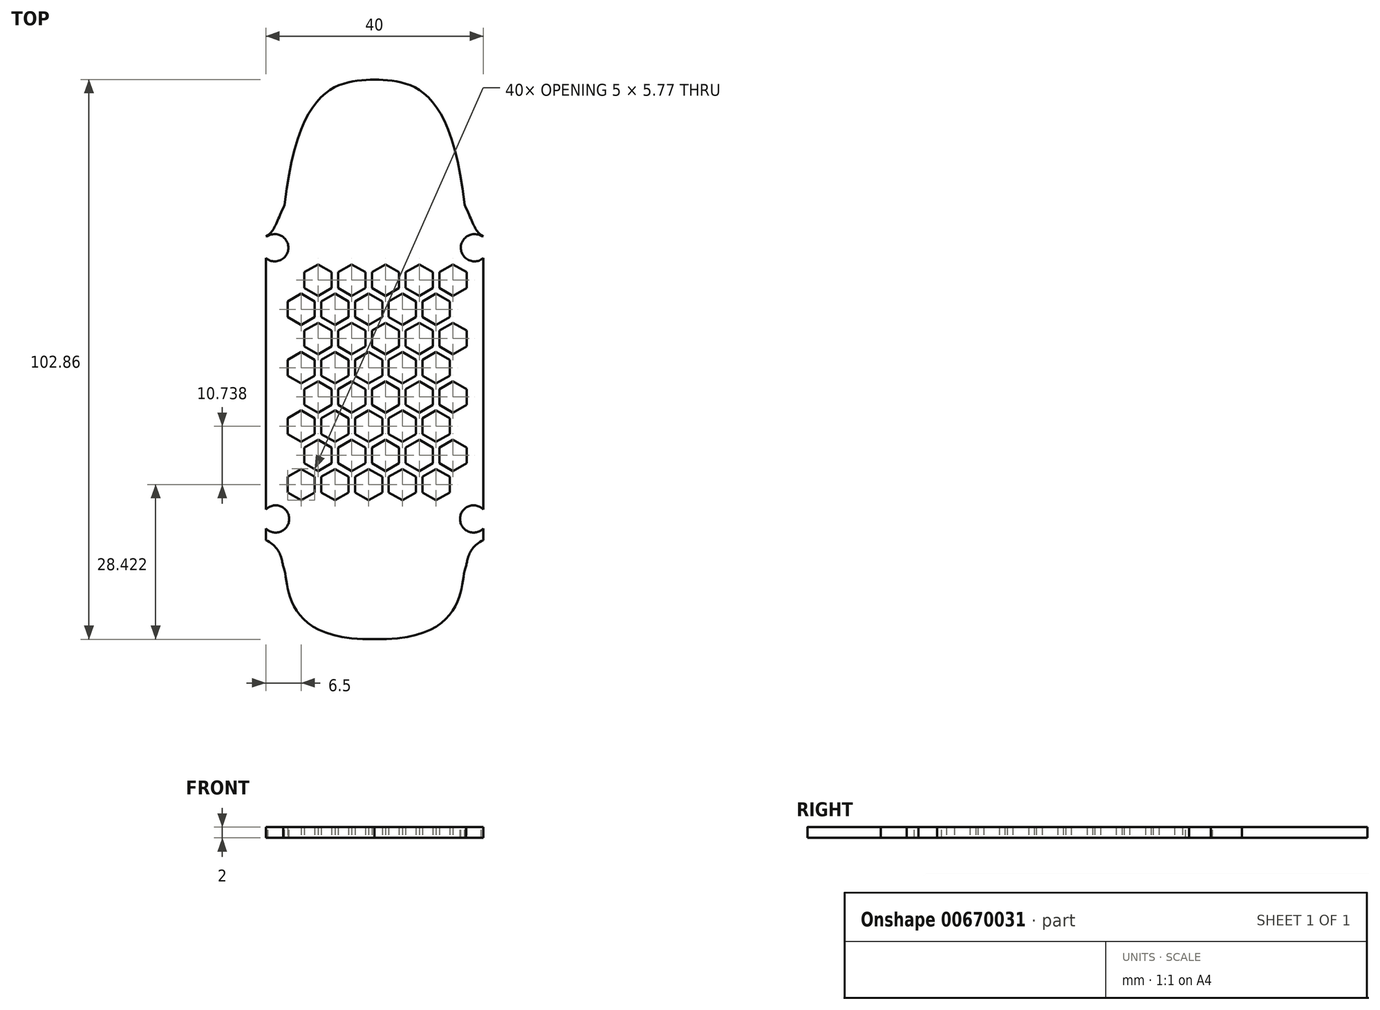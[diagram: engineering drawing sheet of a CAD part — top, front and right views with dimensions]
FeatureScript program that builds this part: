
annotation { "Feature Type Name" : "Feature", "Feature Type Description" : "" }
export const myFeature = defineFeature(function(context is Context, id is Id, definition is map)
    precondition{}
    {
        {
            var Q0;
            Q0=qCreatedBy(makeId("Top.planeOp"),FACE);
            var sketch = newSketch(context, id + "F0", { "sketchPlane" : qUnion([Q0])});
            skLineSegment(sketch, "E0", {"start": v(20, 27.95) * mm, "end": v(20, -27.95) * mm});
            skLineSegment(sketch, "E1", {"start": v(20, -27.95) * mm, "end": v(-20, -27.95) * mm});
            skLineSegment(sketch, "E2", {"start": v(-20, -27.95) * mm, "end": v(-20, 27.95) * mm});
            skLineSegment(sketch, "E3", {"start": v(-20, 27.95) * mm, "end": v(20, 27.95) * mm});
            skPoint(sketch, "E4", {"position": v(0, 0) * mm});
            skPoint(sketch, "E4.positionSnap0", {"position": v(0, 27.95) * mm});
            skPoint(sketch, "E5", {"position": v(-20, 0) * mm});
            skFitSpline(sketch, "E6", {"points": [v(0, 56.71) * mm, v(-16.53, 33.68) * mm], "startDerivative": vector(-17.27, -1.25) * mm, "endDerivative": vector(-7.65, -70.35) * mm});
            skFitSpline(sketch, "E7", {"points": [v(-16.53, 33.68) * mm, v(-20, 27.95) * mm], "startDerivative": vector(-5.62, -11.68) * mm, "endDerivative": vector(-4.8, -2.18) * mm});
            skLineSegment(sketch, "E8", {"start": v(0, 60.75) * mm, "end": v(0, -48.18) * mm, "construction": true});
            skFitSpline(sketch, "E9.MirrorCS", {"points": [v(0, 56.71) * mm, v(16.53, 33.68) * mm], "startDerivative": vector(17.27, -1.25) * mm, "endDerivative": vector(7.65, -70.35) * mm});
            skFitSpline(sketch, "E10.MirrorCS", {"points": [v(16.53, 33.68) * mm, v(20, 27.95) * mm], "startDerivative": vector(5.62, -11.68) * mm, "endDerivative": vector(4.8, -2.18) * mm});
            skFitSpline(sketch, "E11", {"points": [v(20, -27.95) * mm, v(16.8, -32.7) * mm], "startDerivative": vector(-8.06, -3.46) * mm, "endDerivative": vector(-0.94, -3.81) * mm});
            skFitSpline(sketch, "E12", {"points": [v(16.8, -32.7) * mm, v(0, -46.14) * mm], "startDerivative": vector(-3.62, -7.41) * mm, "endDerivative": vector(-53.21, 1.16) * mm});
            skFitSpline(sketch, "E13.MirrorCS", {"points": [v(-16.8, -32.7) * mm, v(0, -46.14) * mm], "startDerivative": vector(3.62, -7.41) * mm, "endDerivative": vector(53.21, 1.16) * mm});
            skFitSpline(sketch, "E14.MirrorCS", {"points": [v(-20, -27.95) * mm, v(-16.8, -32.7) * mm], "startDerivative": vector(8.06, -3.46) * mm, "endDerivative": vector(0.94, -3.81) * mm});
            skCircle(sketch, "E15", {"center": v(18.34, 25.8) * mm, "radius": 2.5 * mm});
            skCircle(sketch, "E16.MirrorC", {"center": v(-18.34, 25.8) * mm, "radius": 2.5 * mm});
            skCircle(sketch, "E17", {"center": v(18.2, -24.04) * mm, "radius": 2.5 * mm});
            skCircle(sketch, "E18.MirrorC", {"center": v(-18.2, -24.04) * mm, "radius": 2.5 * mm});
            skSolve(sketch);
        }
        {
            var Q0;
            Q0=makeQuery(id+"F0.imprint","IMPRINT",FACE,{"disambiguationData":[TD([[makeQuery(id+"F0.imprint","IMPRINT",EDGE,{"derivedFrom":sQuery(id+"F0.wireOp",EDGE,"E1")}),1.0]])]});
            var Q1;
            Q1=makeQuery(id+"F0.imprint","IMPRINT",FACE,{"disambiguationData":[TD([[makeQuery(id+"F0.imprint","IMPRINT",EDGE,{"derivedFrom":sQuery(id+"F0.wireOp",EDGE,"E3")}),1.0]])]});
            var Q2;
            {var subQ1=sQuery(id+"F0.wireOp",EDGE,"E1");Q2=makeQuery(id+"F0.imprint","IMPRINT",FACE,{"disambiguationData":[TD([[makeQuery(id+"F0.imprint","IMPRINT",EDGE,{"derivedFrom":subQ1}),-1.0]])]});}
            extrude(context, id + "F1", {"entities" : qUnion([Q0, Q1, Q2]), "oppositeDirection" : true, "depth" : 2 * mm, "offsetDistance" : 25 * mm});
        }
        {
            var Q0;
            Q0=makeQuery(id+"F1.opExtrude","CAP_FACE",FACE,{"disambiguationData":[OSD([sQuery(id+"F0.wireOp",EDGE,"E0"),sQuery(id+"F0.wireOp",EDGE,"E2"),sQuery(id+"F0.wireOp",EDGE,"E3"),sQuery(id+"F0.wireOp",EDGE,"E6"),sQuery(id+"F0.wireOp",EDGE,"E7"),sQuery(id+"F0.wireOp",EDGE,"E9.MirrorCS"),sQuery(id+"F0.wireOp",EDGE,"E10.MirrorCS"),sQuery(id+"F0.wireOp",EDGE,"E11"),sQuery(id+"F0.wireOp",EDGE,"E12"),sQuery(id+"F0.wireOp",EDGE,"E13.MirrorCS"),sQuery(id+"F0.wireOp",EDGE,"E14.MirrorCS"),sQuery(id+"F0.wireOp",EDGE,"E15"),sQuery(id+"F0.wireOp",EDGE,"E16.MirrorC"),sQuery(id+"F0.wireOp",EDGE,"E17"),sQuery(id+"F0.wireOp",EDGE,"E18.MirrorC")])],"isStart":false});
            var sketch = newSketch(context, id + "F2", { "sketchPlane" : qUnion([Q0])});
            skCircle(sketch, "E19.cCircle", {"center": v(-13.5, 17.73) * mm, "radius": 2.5 * mm, "construction": true});
            skLineSegment(sketch, "E19.0", {"start": v(-11, 19.17) * mm, "end": v(-11, 16.28) * mm});
            skLineSegment(sketch, "E19.1", {"start": v(-11, 16.28) * mm, "end": v(-13.5, 14.84) * mm});
            skLineSegment(sketch, "E19.2", {"start": v(-13.5, 14.84) * mm, "end": v(-16, 16.28) * mm});
            skLineSegment(sketch, "E19.3", {"start": v(-16, 16.28) * mm, "end": v(-16, 19.17) * mm});
            skLineSegment(sketch, "E19.4", {"start": v(-16, 19.17) * mm, "end": v(-13.5, 20.62) * mm});
            skLineSegment(sketch, "E19.5", {"start": v(-13.5, 20.62) * mm, "end": v(-11, 19.17) * mm});
            skPoint(sketch, "E19.0.midPoint", {"position": v(-11, 17.73) * mm});
            skCircle(sketch, "E20.cCircle", {"center": v(-10.4, 12.36) * mm, "radius": 2.5 * mm, "construction": true});
            skLineSegment(sketch, "E20.0", {"start": v(-7.9, 13.8) * mm, "end": v(-7.9, 10.92) * mm});
            skLineSegment(sketch, "E20.1", {"start": v(-7.9, 10.92) * mm, "end": v(-10.4, 9.47) * mm});
            skLineSegment(sketch, "E20.2", {"start": v(-10.4, 9.47) * mm, "end": v(-12.9, 10.92) * mm});
            skLineSegment(sketch, "E20.3", {"start": v(-12.9, 10.92) * mm, "end": v(-12.9, 13.8) * mm});
            skLineSegment(sketch, "E20.4", {"start": v(-12.9, 13.8) * mm, "end": v(-10.4, 15.25) * mm});
            skLineSegment(sketch, "E20.5", {"start": v(-10.4, 15.25) * mm, "end": v(-7.9, 13.8) * mm});
            skPoint(sketch, "E20.0.midPoint", {"position": v(-7.9, 12.36) * mm});
            skCircle(sketch, "E21.0.1.0", {"center": v(-10.4, 1.62) * mm, "radius": 2.5 * mm, "construction": true});
            skCircle(sketch, "E21.0.1.1", {"center": v(-13.5, 7) * mm, "radius": 2.5 * mm, "construction": true});
            skLineSegment(sketch, "E21.0.1.2", {"start": v(-11, 8.43) * mm, "end": v(-11, 5.55) * mm});
            skLineSegment(sketch, "E21.0.1.3", {"start": v(-11, 5.55) * mm, "end": v(-13.5, 4.1) * mm});
            skLineSegment(sketch, "E21.0.1.4", {"start": v(-13.5, 4.1) * mm, "end": v(-16, 5.55) * mm});
            skLineSegment(sketch, "E21.0.1.5", {"start": v(-16, 5.55) * mm, "end": v(-16, 8.43) * mm});
            skLineSegment(sketch, "E21.0.1.6", {"start": v(-16, 8.43) * mm, "end": v(-13.5, 9.88) * mm});
            skLineSegment(sketch, "E21.0.1.7", {"start": v(-13.5, 9.88) * mm, "end": v(-11, 8.43) * mm});
            skLineSegment(sketch, "E21.0.1.8", {"start": v(-7.9, 0.18) * mm, "end": v(-10.4, -1.27) * mm});
            skLineSegment(sketch, "E21.0.1.9", {"start": v(-10.4, -1.27) * mm, "end": v(-12.9, 0.18) * mm});
            skLineSegment(sketch, "E21.0.1.10", {"start": v(-12.9, 3.06) * mm, "end": v(-10.4, 4.5) * mm});
            skPoint(sketch, "E21.0.1.11", {"position": v(-7.9, 1.62) * mm});
            skPoint(sketch, "E21.0.1.12", {"position": v(-11, 7) * mm});
            skLineSegment(sketch, "E21.0.1.13", {"start": v(-10.4, 4.5) * mm, "end": v(-7.9, 3.06) * mm});
            skLineSegment(sketch, "E21.0.1.14", {"start": v(-7.9, 3.06) * mm, "end": v(-7.9, 0.18) * mm});
            skLineSegment(sketch, "E21.0.1.15", {"start": v(-12.9, 0.18) * mm, "end": v(-12.9, 3.06) * mm});
            skCircle(sketch, "E21.0.2.0", {"center": v(-10.4, -9.12) * mm, "radius": 2.5 * mm, "construction": true});
            skCircle(sketch, "E21.0.2.1", {"center": v(-13.5, -3.75) * mm, "radius": 2.5 * mm, "construction": true});
            skLineSegment(sketch, "E21.0.2.2", {"start": v(-11, -2.3) * mm, "end": v(-11, -5.2) * mm});
            skLineSegment(sketch, "E21.0.2.3", {"start": v(-11, -5.2) * mm, "end": v(-13.5, -6.63) * mm});
            skLineSegment(sketch, "E21.0.2.4", {"start": v(-13.5, -6.63) * mm, "end": v(-16, -5.2) * mm});
            skLineSegment(sketch, "E21.0.2.5", {"start": v(-16, -5.2) * mm, "end": v(-16, -2.3) * mm});
            skLineSegment(sketch, "E21.0.2.6", {"start": v(-16, -2.3) * mm, "end": v(-13.5, -0.86) * mm});
            skLineSegment(sketch, "E21.0.2.7", {"start": v(-13.5, -0.86) * mm, "end": v(-11, -2.3) * mm});
            skLineSegment(sketch, "E21.0.2.8", {"start": v(-7.9, -10.56) * mm, "end": v(-10.4, -12) * mm});
            skLineSegment(sketch, "E21.0.2.9", {"start": v(-10.4, -12) * mm, "end": v(-12.9, -10.56) * mm});
            skLineSegment(sketch, "E21.0.2.10", {"start": v(-12.9, -7.67) * mm, "end": v(-10.4, -6.23) * mm});
            skPoint(sketch, "E21.0.2.11", {"position": v(-7.9, -9.12) * mm});
            skPoint(sketch, "E21.0.2.12", {"position": v(-11, -3.75) * mm});
            skLineSegment(sketch, "E21.0.2.13", {"start": v(-10.4, -6.23) * mm, "end": v(-7.9, -7.67) * mm});
            skLineSegment(sketch, "E21.0.2.14", {"start": v(-7.9, -7.67) * mm, "end": v(-7.9, -10.56) * mm});
            skLineSegment(sketch, "E21.0.2.15", {"start": v(-12.9, -10.56) * mm, "end": v(-12.9, -7.67) * mm});
            skCircle(sketch, "E21.0.3.0", {"center": v(-10.4, -19.86) * mm, "radius": 2.5 * mm, "construction": true});
            skCircle(sketch, "E21.0.3.1", {"center": v(-13.5, -14.49) * mm, "radius": 2.5 * mm, "construction": true});
            skLineSegment(sketch, "E21.0.3.2", {"start": v(-11, -13.04) * mm, "end": v(-11, -15.93) * mm});
            skLineSegment(sketch, "E21.0.3.3", {"start": v(-11, -15.93) * mm, "end": v(-13.5, -17.37) * mm});
            skLineSegment(sketch, "E21.0.3.4", {"start": v(-13.5, -17.37) * mm, "end": v(-16, -15.93) * mm});
            skLineSegment(sketch, "E21.0.3.5", {"start": v(-16, -15.93) * mm, "end": v(-16, -13.04) * mm});
            skLineSegment(sketch, "E21.0.3.6", {"start": v(-16, -13.04) * mm, "end": v(-13.5, -11.6) * mm});
            skLineSegment(sketch, "E21.0.3.7", {"start": v(-13.5, -11.6) * mm, "end": v(-11, -13.04) * mm});
            skLineSegment(sketch, "E21.0.3.8", {"start": v(-7.9, -21.3) * mm, "end": v(-10.4, -22.74) * mm});
            skLineSegment(sketch, "E21.0.3.9", {"start": v(-10.4, -22.74) * mm, "end": v(-12.9, -21.3) * mm});
            skLineSegment(sketch, "E21.0.3.10", {"start": v(-12.9, -18.41) * mm, "end": v(-10.4, -16.97) * mm});
            skPoint(sketch, "E21.0.3.11", {"position": v(-7.9, -19.86) * mm});
            skPoint(sketch, "E21.0.3.12", {"position": v(-11, -14.49) * mm});
            skLineSegment(sketch, "E21.0.3.13", {"start": v(-10.4, -16.97) * mm, "end": v(-7.9, -18.41) * mm});
            skLineSegment(sketch, "E21.0.3.14", {"start": v(-7.9, -18.41) * mm, "end": v(-7.9, -21.3) * mm});
            skLineSegment(sketch, "E21.0.3.15", {"start": v(-12.9, -21.3) * mm, "end": v(-12.9, -18.41) * mm});
            skCircle(sketch, "E21.1.0.0", {"center": v(-4.2, 12.36) * mm, "radius": 2.5 * mm, "construction": true});
            skCircle(sketch, "E21.1.0.1", {"center": v(-7.3, 17.73) * mm, "radius": 2.5 * mm, "construction": true});
            skLineSegment(sketch, "E21.1.0.2", {"start": v(-4.8, 19.17) * mm, "end": v(-4.8, 16.28) * mm});
            skLineSegment(sketch, "E21.1.0.3", {"start": v(-4.8, 16.28) * mm, "end": v(-7.3, 14.84) * mm});
            skLineSegment(sketch, "E21.1.0.4", {"start": v(-7.3, 14.84) * mm, "end": v(-9.8, 16.28) * mm});
            skLineSegment(sketch, "E21.1.0.5", {"start": v(-9.8, 16.28) * mm, "end": v(-9.8, 19.17) * mm});
            skLineSegment(sketch, "E21.1.0.6", {"start": v(-9.8, 19.17) * mm, "end": v(-7.3, 20.62) * mm});
            skLineSegment(sketch, "E21.1.0.7", {"start": v(-7.3, 20.62) * mm, "end": v(-4.8, 19.17) * mm});
            skLineSegment(sketch, "E21.1.0.8", {"start": v(-1.7, 10.92) * mm, "end": v(-4.2, 9.47) * mm});
            skLineSegment(sketch, "E21.1.0.9", {"start": v(-4.2, 9.47) * mm, "end": v(-6.7, 10.92) * mm});
            skLineSegment(sketch, "E21.1.0.10", {"start": v(-6.7, 13.8) * mm, "end": v(-4.2, 15.25) * mm});
            skPoint(sketch, "E21.1.0.11", {"position": v(-1.7, 12.36) * mm});
            skPoint(sketch, "E21.1.0.12", {"position": v(-4.8, 17.73) * mm});
            skLineSegment(sketch, "E21.1.0.13", {"start": v(-4.2, 15.25) * mm, "end": v(-1.7, 13.8) * mm});
            skLineSegment(sketch, "E21.1.0.14", {"start": v(-1.7, 13.8) * mm, "end": v(-1.7, 10.92) * mm});
            skLineSegment(sketch, "E21.1.0.15", {"start": v(-6.7, 10.92) * mm, "end": v(-6.7, 13.8) * mm});
            skCircle(sketch, "E21.1.1.0", {"center": v(-4.2, 1.62) * mm, "radius": 2.5 * mm, "construction": true});
            skCircle(sketch, "E21.1.1.1", {"center": v(-7.3, 7) * mm, "radius": 2.5 * mm, "construction": true});
            skLineSegment(sketch, "E21.1.1.2", {"start": v(-4.8, 8.43) * mm, "end": v(-4.8, 5.55) * mm});
            skLineSegment(sketch, "E21.1.1.3", {"start": v(-4.8, 5.55) * mm, "end": v(-7.3, 4.1) * mm});
            skLineSegment(sketch, "E21.1.1.4", {"start": v(-7.3, 4.1) * mm, "end": v(-9.8, 5.55) * mm});
            skLineSegment(sketch, "E21.1.1.5", {"start": v(-9.8, 5.55) * mm, "end": v(-9.8, 8.43) * mm});
            skLineSegment(sketch, "E21.1.1.6", {"start": v(-9.8, 8.43) * mm, "end": v(-7.3, 9.88) * mm});
            skLineSegment(sketch, "E21.1.1.7", {"start": v(-7.3, 9.88) * mm, "end": v(-4.8, 8.43) * mm});
            skLineSegment(sketch, "E21.1.1.8", {"start": v(-1.7, 0.18) * mm, "end": v(-4.2, -1.27) * mm});
            skLineSegment(sketch, "E21.1.1.9", {"start": v(-4.2, -1.27) * mm, "end": v(-6.7, 0.18) * mm});
            skLineSegment(sketch, "E21.1.1.10", {"start": v(-6.7, 3.06) * mm, "end": v(-4.2, 4.5) * mm});
            skPoint(sketch, "E21.1.1.11", {"position": v(-1.7, 1.62) * mm});
            skPoint(sketch, "E21.1.1.12", {"position": v(-4.8, 7) * mm});
            skLineSegment(sketch, "E21.1.1.13", {"start": v(-4.2, 4.5) * mm, "end": v(-1.7, 3.06) * mm});
            skLineSegment(sketch, "E21.1.1.14", {"start": v(-1.7, 3.06) * mm, "end": v(-1.7, 0.18) * mm});
            skLineSegment(sketch, "E21.1.1.15", {"start": v(-6.7, 0.18) * mm, "end": v(-6.7, 3.06) * mm});
            skCircle(sketch, "E21.1.2.0", {"center": v(-4.2, -9.12) * mm, "radius": 2.5 * mm, "construction": true});
            skCircle(sketch, "E21.1.2.1", {"center": v(-7.3, -3.75) * mm, "radius": 2.5 * mm, "construction": true});
            skLineSegment(sketch, "E21.1.2.2", {"start": v(-4.8, -2.3) * mm, "end": v(-4.8, -5.2) * mm});
            skLineSegment(sketch, "E21.1.2.3", {"start": v(-4.8, -5.2) * mm, "end": v(-7.3, -6.63) * mm});
            skLineSegment(sketch, "E21.1.2.4", {"start": v(-7.3, -6.63) * mm, "end": v(-9.8, -5.2) * mm});
            skLineSegment(sketch, "E21.1.2.5", {"start": v(-9.8, -5.2) * mm, "end": v(-9.8, -2.3) * mm});
            skLineSegment(sketch, "E21.1.2.6", {"start": v(-9.8, -2.3) * mm, "end": v(-7.3, -0.86) * mm});
            skLineSegment(sketch, "E21.1.2.7", {"start": v(-7.3, -0.86) * mm, "end": v(-4.8, -2.3) * mm});
            skLineSegment(sketch, "E21.1.2.8", {"start": v(-1.7, -10.56) * mm, "end": v(-4.2, -12) * mm});
            skLineSegment(sketch, "E21.1.2.9", {"start": v(-4.2, -12) * mm, "end": v(-6.7, -10.56) * mm});
            skLineSegment(sketch, "E21.1.2.10", {"start": v(-6.7, -7.67) * mm, "end": v(-4.2, -6.23) * mm});
            skPoint(sketch, "E21.1.2.11", {"position": v(-1.7, -9.12) * mm});
            skPoint(sketch, "E21.1.2.12", {"position": v(-4.8, -3.75) * mm});
            skLineSegment(sketch, "E21.1.2.13", {"start": v(-4.2, -6.23) * mm, "end": v(-1.7, -7.67) * mm});
            skLineSegment(sketch, "E21.1.2.14", {"start": v(-1.7, -7.67) * mm, "end": v(-1.7, -10.56) * mm});
            skLineSegment(sketch, "E21.1.2.15", {"start": v(-6.7, -10.56) * mm, "end": v(-6.7, -7.67) * mm});
            skCircle(sketch, "E21.1.3.0", {"center": v(-4.2, -19.86) * mm, "radius": 2.5 * mm, "construction": true});
            skCircle(sketch, "E21.1.3.1", {"center": v(-7.3, -14.49) * mm, "radius": 2.5 * mm, "construction": true});
            skLineSegment(sketch, "E21.1.3.2", {"start": v(-4.8, -13.04) * mm, "end": v(-4.8, -15.93) * mm});
            skLineSegment(sketch, "E21.1.3.3", {"start": v(-4.8, -15.93) * mm, "end": v(-7.3, -17.37) * mm});
            skLineSegment(sketch, "E21.1.3.4", {"start": v(-7.3, -17.37) * mm, "end": v(-9.8, -15.93) * mm});
            skLineSegment(sketch, "E21.1.3.5", {"start": v(-9.8, -15.93) * mm, "end": v(-9.8, -13.04) * mm});
            skLineSegment(sketch, "E21.1.3.6", {"start": v(-9.8, -13.04) * mm, "end": v(-7.3, -11.6) * mm});
            skLineSegment(sketch, "E21.1.3.7", {"start": v(-7.3, -11.6) * mm, "end": v(-4.8, -13.04) * mm});
            skLineSegment(sketch, "E21.1.3.8", {"start": v(-1.7, -21.3) * mm, "end": v(-4.2, -22.74) * mm});
            skLineSegment(sketch, "E21.1.3.9", {"start": v(-4.2, -22.74) * mm, "end": v(-6.7, -21.3) * mm});
            skLineSegment(sketch, "E21.1.3.10", {"start": v(-6.7, -18.41) * mm, "end": v(-4.2, -16.97) * mm});
            skPoint(sketch, "E21.1.3.11", {"position": v(-1.7, -19.86) * mm});
            skPoint(sketch, "E21.1.3.12", {"position": v(-4.8, -14.49) * mm});
            skLineSegment(sketch, "E21.1.3.13", {"start": v(-4.2, -16.97) * mm, "end": v(-1.7, -18.41) * mm});
            skLineSegment(sketch, "E21.1.3.14", {"start": v(-1.7, -18.41) * mm, "end": v(-1.7, -21.3) * mm});
            skLineSegment(sketch, "E21.1.3.15", {"start": v(-6.7, -21.3) * mm, "end": v(-6.7, -18.41) * mm});
            skCircle(sketch, "E21.2.0.0", {"center": v(2, 12.36) * mm, "radius": 2.5 * mm, "construction": true});
            skCircle(sketch, "E21.2.0.1", {"center": v(-1.1, 17.73) * mm, "radius": 2.5 * mm, "construction": true});
            skLineSegment(sketch, "E21.2.0.2", {"start": v(1.4, 19.17) * mm, "end": v(1.4, 16.28) * mm});
            skLineSegment(sketch, "E21.2.0.3", {"start": v(1.4, 16.28) * mm, "end": v(-1.1, 14.84) * mm});
            skLineSegment(sketch, "E21.2.0.4", {"start": v(-1.1, 14.84) * mm, "end": v(-3.6, 16.28) * mm});
            skLineSegment(sketch, "E21.2.0.5", {"start": v(-3.6, 16.28) * mm, "end": v(-3.6, 19.17) * mm});
            skLineSegment(sketch, "E21.2.0.6", {"start": v(-3.6, 19.17) * mm, "end": v(-1.1, 20.62) * mm});
            skLineSegment(sketch, "E21.2.0.7", {"start": v(-1.1, 20.62) * mm, "end": v(1.4, 19.17) * mm});
            skLineSegment(sketch, "E21.2.0.8", {"start": v(4.5, 10.92) * mm, "end": v(2, 9.47) * mm});
            skLineSegment(sketch, "E21.2.0.9", {"start": v(2, 9.47) * mm, "end": v(-0.5, 10.92) * mm});
            skLineSegment(sketch, "E21.2.0.10", {"start": v(-0.5, 13.8) * mm, "end": v(2, 15.25) * mm});
            skPoint(sketch, "E21.2.0.11", {"position": v(4.5, 12.36) * mm});
            skPoint(sketch, "E21.2.0.12", {"position": v(1.4, 17.73) * mm});
            skLineSegment(sketch, "E21.2.0.13", {"start": v(2, 15.25) * mm, "end": v(4.5, 13.8) * mm});
            skLineSegment(sketch, "E21.2.0.14", {"start": v(4.5, 13.8) * mm, "end": v(4.5, 10.92) * mm});
            skLineSegment(sketch, "E21.2.0.15", {"start": v(-0.5, 10.92) * mm, "end": v(-0.5, 13.8) * mm});
            skCircle(sketch, "E21.2.1.0", {"center": v(2, 1.62) * mm, "radius": 2.5 * mm, "construction": true});
            skCircle(sketch, "E21.2.1.1", {"center": v(-1.1, 7) * mm, "radius": 2.5 * mm, "construction": true});
            skLineSegment(sketch, "E21.2.1.2", {"start": v(1.4, 8.43) * mm, "end": v(1.4, 5.55) * mm});
            skLineSegment(sketch, "E21.2.1.3", {"start": v(1.4, 5.55) * mm, "end": v(-1.1, 4.1) * mm});
            skLineSegment(sketch, "E21.2.1.4", {"start": v(-1.1, 4.1) * mm, "end": v(-3.6, 5.55) * mm});
            skLineSegment(sketch, "E21.2.1.5", {"start": v(-3.6, 5.55) * mm, "end": v(-3.6, 8.43) * mm});
            skLineSegment(sketch, "E21.2.1.6", {"start": v(-3.6, 8.43) * mm, "end": v(-1.1, 9.88) * mm});
            skLineSegment(sketch, "E21.2.1.7", {"start": v(-1.1, 9.88) * mm, "end": v(1.4, 8.43) * mm});
            skLineSegment(sketch, "E21.2.1.8", {"start": v(4.5, 0.18) * mm, "end": v(2, -1.27) * mm});
            skLineSegment(sketch, "E21.2.1.9", {"start": v(2, -1.27) * mm, "end": v(-0.5, 0.18) * mm});
            skLineSegment(sketch, "E21.2.1.10", {"start": v(-0.5, 3.06) * mm, "end": v(2, 4.5) * mm});
            skPoint(sketch, "E21.2.1.11", {"position": v(4.5, 1.62) * mm});
            skPoint(sketch, "E21.2.1.12", {"position": v(1.4, 7) * mm});
            skLineSegment(sketch, "E21.2.1.13", {"start": v(2, 4.5) * mm, "end": v(4.5, 3.06) * mm});
            skLineSegment(sketch, "E21.2.1.14", {"start": v(4.5, 3.06) * mm, "end": v(4.5, 0.18) * mm});
            skLineSegment(sketch, "E21.2.1.15", {"start": v(-0.5, 0.18) * mm, "end": v(-0.5, 3.06) * mm});
            skCircle(sketch, "E21.2.2.0", {"center": v(2, -9.12) * mm, "radius": 2.5 * mm, "construction": true});
            skCircle(sketch, "E21.2.2.1", {"center": v(-1.1, -3.75) * mm, "radius": 2.5 * mm, "construction": true});
            skLineSegment(sketch, "E21.2.2.2", {"start": v(1.4, -2.3) * mm, "end": v(1.4, -5.2) * mm});
            skLineSegment(sketch, "E21.2.2.3", {"start": v(1.4, -5.2) * mm, "end": v(-1.1, -6.63) * mm});
            skLineSegment(sketch, "E21.2.2.4", {"start": v(-1.1, -6.63) * mm, "end": v(-3.6, -5.2) * mm});
            skLineSegment(sketch, "E21.2.2.5", {"start": v(-3.6, -5.2) * mm, "end": v(-3.6, -2.3) * mm});
            skLineSegment(sketch, "E21.2.2.6", {"start": v(-3.6, -2.3) * mm, "end": v(-1.1, -0.86) * mm});
            skLineSegment(sketch, "E21.2.2.7", {"start": v(-1.1, -0.86) * mm, "end": v(1.4, -2.3) * mm});
            skLineSegment(sketch, "E21.2.2.8", {"start": v(4.5, -10.56) * mm, "end": v(2, -12) * mm});
            skLineSegment(sketch, "E21.2.2.9", {"start": v(2, -12) * mm, "end": v(-0.5, -10.56) * mm});
            skLineSegment(sketch, "E21.2.2.10", {"start": v(-0.5, -7.67) * mm, "end": v(2, -6.23) * mm});
            skPoint(sketch, "E21.2.2.11", {"position": v(4.5, -9.12) * mm});
            skPoint(sketch, "E21.2.2.12", {"position": v(1.4, -3.75) * mm});
            skLineSegment(sketch, "E21.2.2.13", {"start": v(2, -6.23) * mm, "end": v(4.5, -7.67) * mm});
            skLineSegment(sketch, "E21.2.2.14", {"start": v(4.5, -7.67) * mm, "end": v(4.5, -10.56) * mm});
            skLineSegment(sketch, "E21.2.2.15", {"start": v(-0.5, -10.56) * mm, "end": v(-0.5, -7.67) * mm});
            skCircle(sketch, "E21.2.3.0", {"center": v(2, -19.86) * mm, "radius": 2.5 * mm, "construction": true});
            skCircle(sketch, "E21.2.3.1", {"center": v(-1.1, -14.49) * mm, "radius": 2.5 * mm, "construction": true});
            skLineSegment(sketch, "E21.2.3.2", {"start": v(1.4, -13.04) * mm, "end": v(1.4, -15.93) * mm});
            skLineSegment(sketch, "E21.2.3.3", {"start": v(1.4, -15.93) * mm, "end": v(-1.1, -17.37) * mm});
            skLineSegment(sketch, "E21.2.3.4", {"start": v(-1.1, -17.37) * mm, "end": v(-3.6, -15.93) * mm});
            skLineSegment(sketch, "E21.2.3.5", {"start": v(-3.6, -15.93) * mm, "end": v(-3.6, -13.04) * mm});
            skLineSegment(sketch, "E21.2.3.6", {"start": v(-3.6, -13.04) * mm, "end": v(-1.1, -11.6) * mm});
            skLineSegment(sketch, "E21.2.3.7", {"start": v(-1.1, -11.6) * mm, "end": v(1.4, -13.04) * mm});
            skLineSegment(sketch, "E21.2.3.8", {"start": v(4.5, -21.3) * mm, "end": v(2, -22.74) * mm});
            skLineSegment(sketch, "E21.2.3.9", {"start": v(2, -22.74) * mm, "end": v(-0.5, -21.3) * mm});
            skLineSegment(sketch, "E21.2.3.10", {"start": v(-0.5, -18.41) * mm, "end": v(2, -16.97) * mm});
            skPoint(sketch, "E21.2.3.11", {"position": v(4.5, -19.86) * mm});
            skPoint(sketch, "E21.2.3.12", {"position": v(1.4, -14.49) * mm});
            skLineSegment(sketch, "E21.2.3.13", {"start": v(2, -16.97) * mm, "end": v(4.5, -18.41) * mm});
            skLineSegment(sketch, "E21.2.3.14", {"start": v(4.5, -18.41) * mm, "end": v(4.5, -21.3) * mm});
            skLineSegment(sketch, "E21.2.3.15", {"start": v(-0.5, -21.3) * mm, "end": v(-0.5, -18.41) * mm});
            skCircle(sketch, "E21.3.0.0", {"center": v(8.2, 12.36) * mm, "radius": 2.5 * mm, "construction": true});
            skCircle(sketch, "E21.3.0.1", {"center": v(5.1, 17.73) * mm, "radius": 2.5 * mm, "construction": true});
            skLineSegment(sketch, "E21.3.0.2", {"start": v(7.6, 19.17) * mm, "end": v(7.6, 16.28) * mm});
            skLineSegment(sketch, "E21.3.0.3", {"start": v(7.6, 16.28) * mm, "end": v(5.1, 14.84) * mm});
            skLineSegment(sketch, "E21.3.0.4", {"start": v(5.1, 14.84) * mm, "end": v(2.6, 16.28) * mm});
            skLineSegment(sketch, "E21.3.0.5", {"start": v(2.6, 16.28) * mm, "end": v(2.6, 19.17) * mm});
            skLineSegment(sketch, "E21.3.0.6", {"start": v(2.6, 19.17) * mm, "end": v(5.1, 20.62) * mm});
            skLineSegment(sketch, "E21.3.0.7", {"start": v(5.1, 20.62) * mm, "end": v(7.6, 19.17) * mm});
            skLineSegment(sketch, "E21.3.0.8", {"start": v(10.7, 10.92) * mm, "end": v(8.2, 9.47) * mm});
            skLineSegment(sketch, "E21.3.0.9", {"start": v(8.2, 9.47) * mm, "end": v(5.7, 10.92) * mm});
            skLineSegment(sketch, "E21.3.0.10", {"start": v(5.7, 13.8) * mm, "end": v(8.2, 15.25) * mm});
            skPoint(sketch, "E21.3.0.11", {"position": v(10.7, 12.36) * mm});
            skPoint(sketch, "E21.3.0.12", {"position": v(7.6, 17.73) * mm});
            skLineSegment(sketch, "E21.3.0.13", {"start": v(8.2, 15.25) * mm, "end": v(10.7, 13.8) * mm});
            skLineSegment(sketch, "E21.3.0.14", {"start": v(10.7, 13.8) * mm, "end": v(10.7, 10.92) * mm});
            skLineSegment(sketch, "E21.3.0.15", {"start": v(5.7, 10.92) * mm, "end": v(5.7, 13.8) * mm});
            skCircle(sketch, "E21.3.1.0", {"center": v(8.2, 1.62) * mm, "radius": 2.5 * mm, "construction": true});
            skCircle(sketch, "E21.3.1.1", {"center": v(5.1, 7) * mm, "radius": 2.5 * mm, "construction": true});
            skLineSegment(sketch, "E21.3.1.2", {"start": v(7.6, 8.43) * mm, "end": v(7.6, 5.55) * mm});
            skLineSegment(sketch, "E21.3.1.3", {"start": v(7.6, 5.55) * mm, "end": v(5.1, 4.1) * mm});
            skLineSegment(sketch, "E21.3.1.4", {"start": v(5.1, 4.1) * mm, "end": v(2.6, 5.55) * mm});
            skLineSegment(sketch, "E21.3.1.5", {"start": v(2.6, 5.55) * mm, "end": v(2.6, 8.43) * mm});
            skLineSegment(sketch, "E21.3.1.6", {"start": v(2.6, 8.43) * mm, "end": v(5.1, 9.88) * mm});
            skLineSegment(sketch, "E21.3.1.7", {"start": v(5.1, 9.88) * mm, "end": v(7.6, 8.43) * mm});
            skLineSegment(sketch, "E21.3.1.8", {"start": v(10.7, 0.18) * mm, "end": v(8.2, -1.27) * mm});
            skLineSegment(sketch, "E21.3.1.9", {"start": v(8.2, -1.27) * mm, "end": v(5.7, 0.18) * mm});
            skLineSegment(sketch, "E21.3.1.10", {"start": v(5.7, 3.06) * mm, "end": v(8.2, 4.5) * mm});
            skPoint(sketch, "E21.3.1.11", {"position": v(10.7, 1.62) * mm});
            skPoint(sketch, "E21.3.1.12", {"position": v(7.6, 7) * mm});
            skLineSegment(sketch, "E21.3.1.13", {"start": v(8.2, 4.5) * mm, "end": v(10.7, 3.06) * mm});
            skLineSegment(sketch, "E21.3.1.14", {"start": v(10.7, 3.06) * mm, "end": v(10.7, 0.18) * mm});
            skLineSegment(sketch, "E21.3.1.15", {"start": v(5.7, 0.18) * mm, "end": v(5.7, 3.06) * mm});
            skCircle(sketch, "E21.3.2.0", {"center": v(8.2, -9.12) * mm, "radius": 2.5 * mm, "construction": true});
            skCircle(sketch, "E21.3.2.1", {"center": v(5.1, -3.75) * mm, "radius": 2.5 * mm, "construction": true});
            skLineSegment(sketch, "E21.3.2.2", {"start": v(7.6, -2.3) * mm, "end": v(7.6, -5.2) * mm});
            skLineSegment(sketch, "E21.3.2.3", {"start": v(7.6, -5.2) * mm, "end": v(5.1, -6.63) * mm});
            skLineSegment(sketch, "E21.3.2.4", {"start": v(5.1, -6.63) * mm, "end": v(2.6, -5.2) * mm});
            skLineSegment(sketch, "E21.3.2.5", {"start": v(2.6, -5.2) * mm, "end": v(2.6, -2.3) * mm});
            skLineSegment(sketch, "E21.3.2.6", {"start": v(2.6, -2.3) * mm, "end": v(5.1, -0.86) * mm});
            skLineSegment(sketch, "E21.3.2.7", {"start": v(5.1, -0.86) * mm, "end": v(7.6, -2.3) * mm});
            skLineSegment(sketch, "E21.3.2.8", {"start": v(10.7, -10.56) * mm, "end": v(8.2, -12) * mm});
            skLineSegment(sketch, "E21.3.2.9", {"start": v(8.2, -12) * mm, "end": v(5.7, -10.56) * mm});
            skLineSegment(sketch, "E21.3.2.10", {"start": v(5.7, -7.67) * mm, "end": v(8.2, -6.23) * mm});
            skPoint(sketch, "E21.3.2.11", {"position": v(10.7, -9.12) * mm});
            skPoint(sketch, "E21.3.2.12", {"position": v(7.6, -3.75) * mm});
            skLineSegment(sketch, "E21.3.2.13", {"start": v(8.2, -6.23) * mm, "end": v(10.7, -7.67) * mm});
            skLineSegment(sketch, "E21.3.2.14", {"start": v(10.7, -7.67) * mm, "end": v(10.7, -10.56) * mm});
            skLineSegment(sketch, "E21.3.2.15", {"start": v(5.7, -10.56) * mm, "end": v(5.7, -7.67) * mm});
            skCircle(sketch, "E21.3.3.0", {"center": v(8.2, -19.86) * mm, "radius": 2.5 * mm, "construction": true});
            skCircle(sketch, "E21.3.3.1", {"center": v(5.1, -14.49) * mm, "radius": 2.5 * mm, "construction": true});
            skLineSegment(sketch, "E21.3.3.2", {"start": v(7.6, -13.04) * mm, "end": v(7.6, -15.93) * mm});
            skLineSegment(sketch, "E21.3.3.3", {"start": v(7.6, -15.93) * mm, "end": v(5.1, -17.37) * mm});
            skLineSegment(sketch, "E21.3.3.4", {"start": v(5.1, -17.37) * mm, "end": v(2.6, -15.93) * mm});
            skLineSegment(sketch, "E21.3.3.5", {"start": v(2.6, -15.93) * mm, "end": v(2.6, -13.04) * mm});
            skLineSegment(sketch, "E21.3.3.6", {"start": v(2.6, -13.04) * mm, "end": v(5.1, -11.6) * mm});
            skLineSegment(sketch, "E21.3.3.7", {"start": v(5.1, -11.6) * mm, "end": v(7.6, -13.04) * mm});
            skLineSegment(sketch, "E21.3.3.8", {"start": v(10.7, -21.3) * mm, "end": v(8.2, -22.74) * mm});
            skLineSegment(sketch, "E21.3.3.9", {"start": v(8.2, -22.74) * mm, "end": v(5.7, -21.3) * mm});
            skLineSegment(sketch, "E21.3.3.10", {"start": v(5.7, -18.41) * mm, "end": v(8.2, -16.97) * mm});
            skPoint(sketch, "E21.3.3.11", {"position": v(10.7, -19.86) * mm});
            skPoint(sketch, "E21.3.3.12", {"position": v(7.6, -14.49) * mm});
            skLineSegment(sketch, "E21.3.3.13", {"start": v(8.2, -16.97) * mm, "end": v(10.7, -18.41) * mm});
            skLineSegment(sketch, "E21.3.3.14", {"start": v(10.7, -18.41) * mm, "end": v(10.7, -21.3) * mm});
            skLineSegment(sketch, "E21.3.3.15", {"start": v(5.7, -21.3) * mm, "end": v(5.7, -18.41) * mm});
            skCircle(sketch, "E21.4.0.0", {"center": v(14.4, 12.36) * mm, "radius": 2.5 * mm, "construction": true});
            skCircle(sketch, "E21.4.0.1", {"center": v(11.3, 17.73) * mm, "radius": 2.5 * mm, "construction": true});
            skLineSegment(sketch, "E21.4.0.2", {"start": v(13.8, 19.17) * mm, "end": v(13.8, 16.28) * mm});
            skLineSegment(sketch, "E21.4.0.3", {"start": v(13.8, 16.28) * mm, "end": v(11.3, 14.84) * mm});
            skLineSegment(sketch, "E21.4.0.4", {"start": v(11.3, 14.84) * mm, "end": v(8.8, 16.28) * mm});
            skLineSegment(sketch, "E21.4.0.5", {"start": v(8.8, 16.28) * mm, "end": v(8.8, 19.17) * mm});
            skLineSegment(sketch, "E21.4.0.6", {"start": v(8.8, 19.17) * mm, "end": v(11.3, 20.62) * mm});
            skLineSegment(sketch, "E21.4.0.7", {"start": v(11.3, 20.62) * mm, "end": v(13.8, 19.17) * mm});
            skLineSegment(sketch, "E21.4.0.8", {"start": v(16.9, 10.92) * mm, "end": v(14.4, 9.47) * mm});
            skLineSegment(sketch, "E21.4.0.9", {"start": v(14.4, 9.47) * mm, "end": v(11.9, 10.92) * mm});
            skLineSegment(sketch, "E21.4.0.10", {"start": v(11.9, 13.8) * mm, "end": v(14.4, 15.25) * mm});
            skPoint(sketch, "E21.4.0.11", {"position": v(16.9, 12.36) * mm});
            skPoint(sketch, "E21.4.0.12", {"position": v(13.8, 17.73) * mm});
            skLineSegment(sketch, "E21.4.0.13", {"start": v(14.4, 15.25) * mm, "end": v(16.9, 13.8) * mm});
            skLineSegment(sketch, "E21.4.0.14", {"start": v(16.9, 13.8) * mm, "end": v(16.9, 10.92) * mm});
            skLineSegment(sketch, "E21.4.0.15", {"start": v(11.9, 10.92) * mm, "end": v(11.9, 13.8) * mm});
            skCircle(sketch, "E21.4.1.0", {"center": v(14.4, 1.62) * mm, "radius": 2.5 * mm, "construction": true});
            skCircle(sketch, "E21.4.1.1", {"center": v(11.3, 7) * mm, "radius": 2.5 * mm, "construction": true});
            skLineSegment(sketch, "E21.4.1.2", {"start": v(13.8, 8.43) * mm, "end": v(13.8, 5.55) * mm});
            skLineSegment(sketch, "E21.4.1.3", {"start": v(13.8, 5.55) * mm, "end": v(11.3, 4.1) * mm});
            skLineSegment(sketch, "E21.4.1.4", {"start": v(11.3, 4.1) * mm, "end": v(8.8, 5.55) * mm});
            skLineSegment(sketch, "E21.4.1.5", {"start": v(8.8, 5.55) * mm, "end": v(8.8, 8.43) * mm});
            skLineSegment(sketch, "E21.4.1.6", {"start": v(8.8, 8.43) * mm, "end": v(11.3, 9.88) * mm});
            skLineSegment(sketch, "E21.4.1.7", {"start": v(11.3, 9.88) * mm, "end": v(13.8, 8.43) * mm});
            skLineSegment(sketch, "E21.4.1.8", {"start": v(16.9, 0.18) * mm, "end": v(14.4, -1.27) * mm});
            skLineSegment(sketch, "E21.4.1.9", {"start": v(14.4, -1.27) * mm, "end": v(11.9, 0.18) * mm});
            skLineSegment(sketch, "E21.4.1.10", {"start": v(11.9, 3.06) * mm, "end": v(14.4, 4.5) * mm});
            skPoint(sketch, "E21.4.1.11", {"position": v(16.9, 1.62) * mm});
            skPoint(sketch, "E21.4.1.12", {"position": v(13.8, 7) * mm});
            skLineSegment(sketch, "E21.4.1.13", {"start": v(14.4, 4.5) * mm, "end": v(16.9, 3.06) * mm});
            skLineSegment(sketch, "E21.4.1.14", {"start": v(16.9, 3.06) * mm, "end": v(16.9, 0.18) * mm});
            skLineSegment(sketch, "E21.4.1.15", {"start": v(11.9, 0.18) * mm, "end": v(11.9, 3.06) * mm});
            skCircle(sketch, "E21.4.2.0", {"center": v(14.4, -9.12) * mm, "radius": 2.5 * mm, "construction": true});
            skCircle(sketch, "E21.4.2.1", {"center": v(11.3, -3.75) * mm, "radius": 2.5 * mm, "construction": true});
            skLineSegment(sketch, "E21.4.2.2", {"start": v(13.8, -2.3) * mm, "end": v(13.8, -5.2) * mm});
            skLineSegment(sketch, "E21.4.2.3", {"start": v(13.8, -5.2) * mm, "end": v(11.3, -6.63) * mm});
            skLineSegment(sketch, "E21.4.2.4", {"start": v(11.3, -6.63) * mm, "end": v(8.8, -5.2) * mm});
            skLineSegment(sketch, "E21.4.2.5", {"start": v(8.8, -5.2) * mm, "end": v(8.8, -2.3) * mm});
            skLineSegment(sketch, "E21.4.2.6", {"start": v(8.8, -2.3) * mm, "end": v(11.3, -0.86) * mm});
            skLineSegment(sketch, "E21.4.2.7", {"start": v(11.3, -0.86) * mm, "end": v(13.8, -2.3) * mm});
            skLineSegment(sketch, "E21.4.2.8", {"start": v(16.9, -10.56) * mm, "end": v(14.4, -12) * mm});
            skLineSegment(sketch, "E21.4.2.9", {"start": v(14.4, -12) * mm, "end": v(11.9, -10.56) * mm});
            skLineSegment(sketch, "E21.4.2.10", {"start": v(11.9, -7.67) * mm, "end": v(14.4, -6.23) * mm});
            skPoint(sketch, "E21.4.2.11", {"position": v(16.9, -9.12) * mm});
            skPoint(sketch, "E21.4.2.12", {"position": v(13.8, -3.75) * mm});
            skLineSegment(sketch, "E21.4.2.13", {"start": v(14.4, -6.23) * mm, "end": v(16.9, -7.67) * mm});
            skLineSegment(sketch, "E21.4.2.14", {"start": v(16.9, -7.67) * mm, "end": v(16.9, -10.56) * mm});
            skLineSegment(sketch, "E21.4.2.15", {"start": v(11.9, -10.56) * mm, "end": v(11.9, -7.67) * mm});
            skCircle(sketch, "E21.4.3.0", {"center": v(14.4, -19.86) * mm, "radius": 2.5 * mm, "construction": true});
            skCircle(sketch, "E21.4.3.1", {"center": v(11.3, -14.49) * mm, "radius": 2.5 * mm, "construction": true});
            skLineSegment(sketch, "E21.4.3.2", {"start": v(13.8, -13.04) * mm, "end": v(13.8, -15.93) * mm});
            skLineSegment(sketch, "E21.4.3.3", {"start": v(13.8, -15.93) * mm, "end": v(11.3, -17.37) * mm});
            skLineSegment(sketch, "E21.4.3.4", {"start": v(11.3, -17.37) * mm, "end": v(8.8, -15.93) * mm});
            skLineSegment(sketch, "E21.4.3.5", {"start": v(8.8, -15.93) * mm, "end": v(8.8, -13.04) * mm});
            skLineSegment(sketch, "E21.4.3.6", {"start": v(8.8, -13.04) * mm, "end": v(11.3, -11.6) * mm});
            skLineSegment(sketch, "E21.4.3.7", {"start": v(11.3, -11.6) * mm, "end": v(13.8, -13.04) * mm});
            skLineSegment(sketch, "E21.4.3.8", {"start": v(16.9, -21.3) * mm, "end": v(14.4, -22.74) * mm});
            skLineSegment(sketch, "E21.4.3.9", {"start": v(14.4, -22.74) * mm, "end": v(11.9, -21.3) * mm});
            skLineSegment(sketch, "E21.4.3.10", {"start": v(11.9, -18.41) * mm, "end": v(14.4, -16.97) * mm});
            skPoint(sketch, "E21.4.3.11", {"position": v(16.9, -19.86) * mm});
            skPoint(sketch, "E21.4.3.12", {"position": v(13.8, -14.49) * mm});
            skLineSegment(sketch, "E21.4.3.13", {"start": v(14.4, -16.97) * mm, "end": v(16.9, -18.41) * mm});
            skLineSegment(sketch, "E21.4.3.14", {"start": v(16.9, -18.41) * mm, "end": v(16.9, -21.3) * mm});
            skLineSegment(sketch, "E21.4.3.15", {"start": v(11.9, -21.3) * mm, "end": v(11.9, -18.41) * mm});
            skLineSegment(sketch, "E21.direction1", {"start": v(-12.9, 10.92) * mm, "end": v(-6.7, 10.92) * mm, "construction": true});
            skLineSegment(sketch, "E21.direction2", {"start": v(-12.9, 10.92) * mm, "end": v(-12.9, 0.18) * mm, "construction": true});
            skSolve(sketch);
        }
        {
            var Q0;
            Q0 = qSketchRegion(id + "F2", true);
            extrude(context, id + "F3", {"entities" : qUnion([Q0]), "operationType" : NewBodyOperationType.REMOVE, "endBound" : BoundingType.THROUGH_ALL, "oppositeDirection" : true, "depth" : 25 * mm, "offsetDistance" : 25 * mm});
        }
    });
